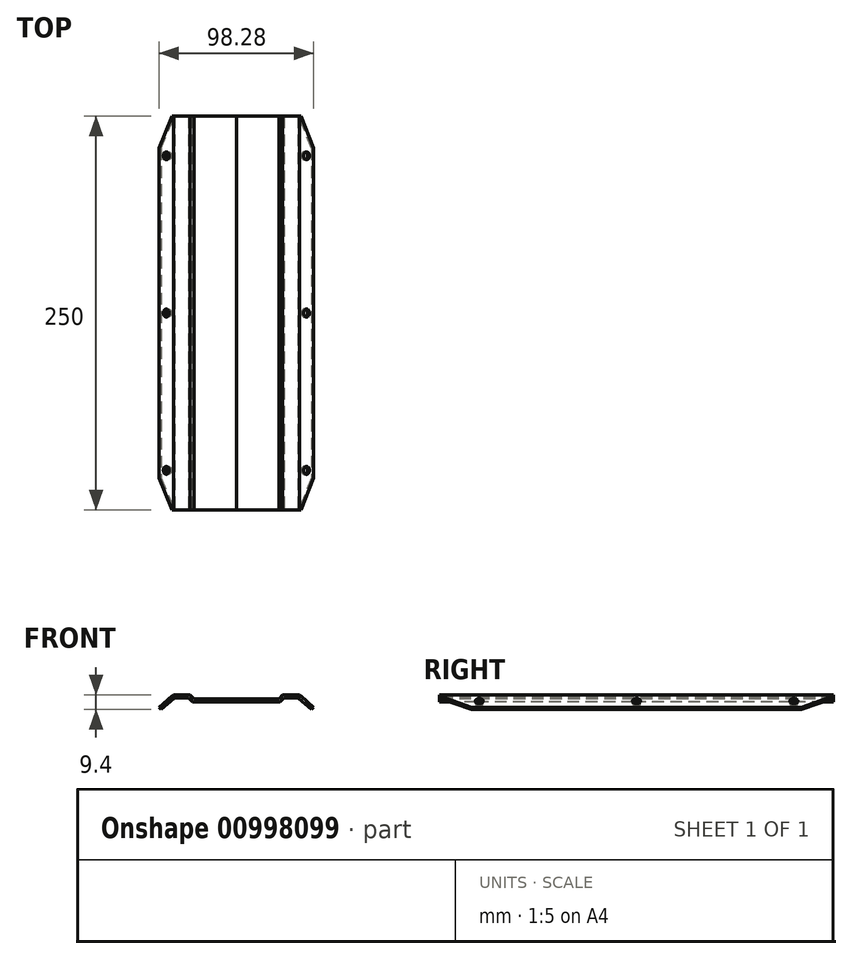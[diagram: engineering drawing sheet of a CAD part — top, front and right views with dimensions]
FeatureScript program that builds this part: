
annotation { "Feature Type Name" : "Feature", "Feature Type Description" : "" }
export const myFeature = defineFeature(function(context is Context, id is Id, definition is map)
    precondition{}
    {
        {
            var Q0;
            Q0=qCreatedBy(makeId("Front.planeOp"),FACE);
            var sketch = newSketch(context, id + "F0", { "sketchPlane" : qUnion([Q0])});
            skLineSegment(sketch, "E0.MirrorCS", {"start": v(-40, -5.5) * mm, "end": v(-49.14, -13.42) * mm});
            skLineSegment(sketch, "E1", {"start": v(0, -293.98) * mm, "end": v(0, 32.01) * mm, "construction": true});
            skLineSegment(sketch, "E2", {"start": v(-40, -5.5) * mm, "end": v(-29.47, -5.5) * mm});
            skLineSegment(sketch, "E3", {"start": v(-27.8, -9.95) * mm, "end": v(0, -9.95) * mm});
            skLineSegment(sketch, "E4", {"start": v(-27.02, -7.95) * mm, "end": v(0, -7.95) * mm});
            skLineSegment(sketch, "E5", {"start": v(-30.25, -7.5) * mm, "end": v(-39.25, -7.5) * mm});
            skLineSegment(sketch, "E6", {"start": v(-47.8, -14.9) * mm, "end": v(-39.25, -7.5) * mm});
            skLineSegment(sketch, "E7", {"start": v(-49.14, -13.42) * mm, "end": v(-47.8, -14.9) * mm});
            skLineSegment(sketch, "E8", {"start": v(-29.47, -5.5) * mm, "end": v(-27.02, -7.95) * mm});
            skLineSegment(sketch, "E9", {"start": v(-30.25, -7.5) * mm, "end": v(-27.8, -9.95) * mm});
            skLineSegment(sketch, "E10", {"start": v(0, -7.95) * mm, "end": v(0, -9.95) * mm});
            skSolve(sketch);
        }
        {
            var Q0;
            Q0=qCreatedBy(makeId("Right.planeOp"),FACE);
            var sketch = newSketch(context, id + "F1", { "sketchPlane" : qUnion([Q0])});
            skLineSegment(sketch, "E11", {"start": v(0, 0) * mm, "end": v(260, 0) * mm});
            skLineSegment(sketch, "E12", {"start": v(260, 28.78) * mm, "end": v(260, -19.4) * mm, "construction": true});
            skLineSegment(sketch, "E13", {"start": v(212.2, 0) * mm, "end": v(0, 0) * mm});
            skSolve(sketch);
        }
        {
            var Q0;
            Q0=makeQuery(id+"F0.imprint","IMPRINT",FACE,{"disambiguationData":[TD([[makeQuery(id+"F0.imprint","IMPRINT",EDGE,{"derivedFrom":sQuery(id+"F0.wireOp",EDGE,"E0.MirrorCS")}),1.0]])]});
            extrude(context, id + "F2", {"entities" : qUnion([Q0]), "oppositeDirection" : true, "depth" : 250 * mm, "offsetDistance" : 25.4 * mm});
        }
        {
            var Q0;
            Q0=makeQuery(id+"F2.opExtrude","SWEPT_FACE",FACE,{"disambiguationData":[OSD([sQuery(id+"F0.wireOp",EDGE,"E0.MirrorCS")])]});
            var sketch = newSketch(context, id + "F3", { "sketchPlane" : qUnion([Q0])});
            skPoint(sketch, "E14", {"position": v(-39.9, 25.1) * mm});
            skPoint(sketch, "E15.0.1.0", {"position": v(-39.9, 125) * mm});
            skPoint(sketch, "E15.0.2.0", {"position": v(-39.9, 224.9) * mm});
            skLineSegment(sketch, "E15.direction1", {"start": v(-39.9, 25.1) * mm, "end": v(-27.68, 25.1) * mm, "construction": true});
            skLineSegment(sketch, "E15.direction2", {"start": v(-39.9, 25.1) * mm, "end": v(-39.9, 125) * mm, "construction": true});
            skLineSegment(sketch, "E16", {"start": v(-39.9, 250) * mm, "end": v(-39.9, 0) * mm, "construction": true});
            skSolve(sketch);
        }
        {
            var Q0;
            Q0=sQuery(id+"F3.wireOp",VERTEX,"E15.0.2.0");
            var Q1;
            Q1=sQuery(id+"F3.wireOp",VERTEX,"E15.0.1.0");
            var Q2;
            Q2=sQuery(id+"F3.wireOp",VERTEX,"E14");
            var Q3;
            Q3=makeQuery(id+"F2.opExtrude","SWEPT_BODY",BODY,{"disambiguationData":[OSD([sQuery(id+"F0.wireOp",EDGE,"E0.MirrorCS"),sQuery(id+"F0.wireOp",EDGE,"2TKtJtls-HKZL-9pNc-KhSM-2cr5P1jvKiuO"),sQuery(id+"F0.wireOp",EDGE,"E2"),sQuery(id+"F0.wireOp",EDGE,"fDTOxo3d-3rfX-dBY2-zsrn-CqeZibWQkMEg"),sQuery(id+"F0.wireOp",EDGE,"E3"),sQuery(id+"F0.wireOp",EDGE,"5IlnrrRk-z5Vu-BmW8-36St-VWP8HLIqOyHw"),sQuery(id+"F0.wireOp",EDGE,"E4"),sQuery(id+"F0.wireOp",EDGE,"E5"),sQuery(id+"F0.wireOp",EDGE,"ODpkLtvZ-vErJ-WUVO-MY3c-zyF2DTRlXPyZ"),sQuery(id+"F0.wireOp",EDGE,"4b80dda3-bf22-4c31-a00e-16da6902330a0.MirrorCS"),sQuery(id+"F0.wireOp",EDGE,"4b80dda3-bf22-4c31-a00e-16da6902330a1.MirrorCS"),sQuery(id+"F0.wireOp",EDGE,"4b80dda3-bf22-4c31-a00e-16da6902330a2.MirrorCS"),sQuery(id+"F0.wireOp",EDGE,"4b80dda3-bf22-4c31-a00e-16da6902330a3.MirrorCS"),sQuery(id+"F0.wireOp",EDGE,"4b80dda3-bf22-4c31-a00e-16da6902330a4.MirrorCS"),sQuery(id+"F0.wireOp",EDGE,"4b80dda3-bf22-4c31-a00e-16da6902330a5.MirrorCS"),sQuery(id+"F0.wireOp",EDGE,"4b80dda3-bf22-4c31-a00e-16da6902330a6.MirrorCS"),sQuery(id+"F0.wireOp",EDGE,"4b80dda3-bf22-4c31-a00e-16da6902330a7.MirrorCS"),sQuery(id+"F0.wireOp",EDGE,"4b80dda3-bf22-4c31-a00e-16da6902330a8.MirrorCS")])]});
            hole(context, id + "F4", {"style" : HoleStyle.SIMPLE, "endStyle" : HoleEndStyle.THROUGH, "holeDiameter" : 5 * mm, "majorDiameter" : 6.35 * mm, "isTappedThrough" : true, "tappedDepth" : 12.7 * mm, "tapClearance" : 3, "locations" : qUnion([Q0, Q1, Q2]), "scope" : qUnion([Q3])});
        }
        {
            var Q0;
            Q0=makeQuery(id+"F2.opExtrude","SWEPT_FACE",FACE,{"disambiguationData":[OSD([sQuery(id+"F0.wireOp",EDGE,"E0.MirrorCS")])]});
            var sketch = newSketch(context, id + "F5", { "sketchPlane" : qUnion([Q0])});
            skLineSegment(sketch, "E17", {"start": v(-35.03, 250) * mm, "end": v(-45.94, 229.7) * mm});
            skLineSegment(sketch, "E18", {"start": v(-35.03, 0) * mm, "end": v(-45.94, 20.3) * mm});
            skSolve(sketch);
        }
        {
            var Q0;
            {var subQ0=sQuery(id+"F5.wireOp",EDGE,"E17");Q0=makeQuery(id+"F5.imprint","IMPRINT",FACE,{"disambiguationData":[TD([[makeQuery(id+"F5.imprint","IMPRINT",EDGE,{"derivedFrom":subQ0}),-1.0]])]});}
            var Q1;
            {var subQ0=sQuery(id+"F0.wireOp",EDGE,"E0.MirrorCS");var subQ1=makeQuery(id+"F2.opExtrude","CAP_EDGE",EDGE,{"disambiguationData":[OSD([subQ0])],"isStart":true});var subQ4=sQuery(id+"F5.wireOp",EDGE,"E18");var subQ5=makeQuery(id+"F5.imprint","INTERSECT",VERTEX,{"derivedFrom":[subQ1,subQ4]});Q1=makeQuery(id+"F5.imprint","IMPRINT",FACE,{"disambiguationData":[TD([[makeQuery(id+"F5.imprint","IMPRINT",EDGE,{"disambiguationData":[TD([[subQ5,-1.0]])],"derivedFrom":subQ4}),1.0]])]});}
            extrude(context, id + "F6", {"entities" : qUnion([Q0, Q1]), "operationType" : NewBodyOperationType.REMOVE, "endBound" : BoundingType.THROUGH_ALL, "oppositeDirection" : true, "depth" : 25.4 * mm, "offsetDistance" : 25.4 * mm});
        }
        {
            var Q0;
            Q0=sQuery(id+"F1.wireOp",VERTEX,"E11.end");
            var Q1;
            Q1=sQuery(id+"F1.wireOp",VERTEX,"E12.start");
            var Q2;
            Q2=sQuery(id+"F1.wireOp",VERTEX,"E11.start");
            cPlane(context, id + "F7", {"entities" : qUnion([Q0, Q1, Q2]), "cplaneType" : CPlaneType.THREE_POINT, "offset" : 25.4 * mm, "width" : 152.4 * mm, "height" : 152.4 * mm});
        }
        {
            var Q0;
            Q0=makeQuery(id+"F2.opExtrude","SWEPT_BODY",BODY,{"disambiguationData":[OSD([sQuery(id+"F0.wireOp",EDGE,"E0.MirrorCS"),sQuery(id+"F0.wireOp",EDGE,"E2"),sQuery(id+"F0.wireOp",EDGE,"E3"),sQuery(id+"F0.wireOp",EDGE,"E4"),sQuery(id+"F0.wireOp",EDGE,"E5"),sQuery(id+"F0.wireOp",EDGE,"E6"),sQuery(id+"F0.wireOp",EDGE,"E7"),sQuery(id+"F0.wireOp",EDGE,"E8"),sQuery(id+"F0.wireOp",EDGE,"E9"),sQuery(id+"F0.wireOp",EDGE,"E10")])]});
            var Q1;
            Q1=qCreatedBy(id+"F7.planeOp",FACE);
            mirror(context, id + "F8", {"entities" : qUnion([Q0]), "mirrorPlane" : qUnion([Q1])});
        }
    });
